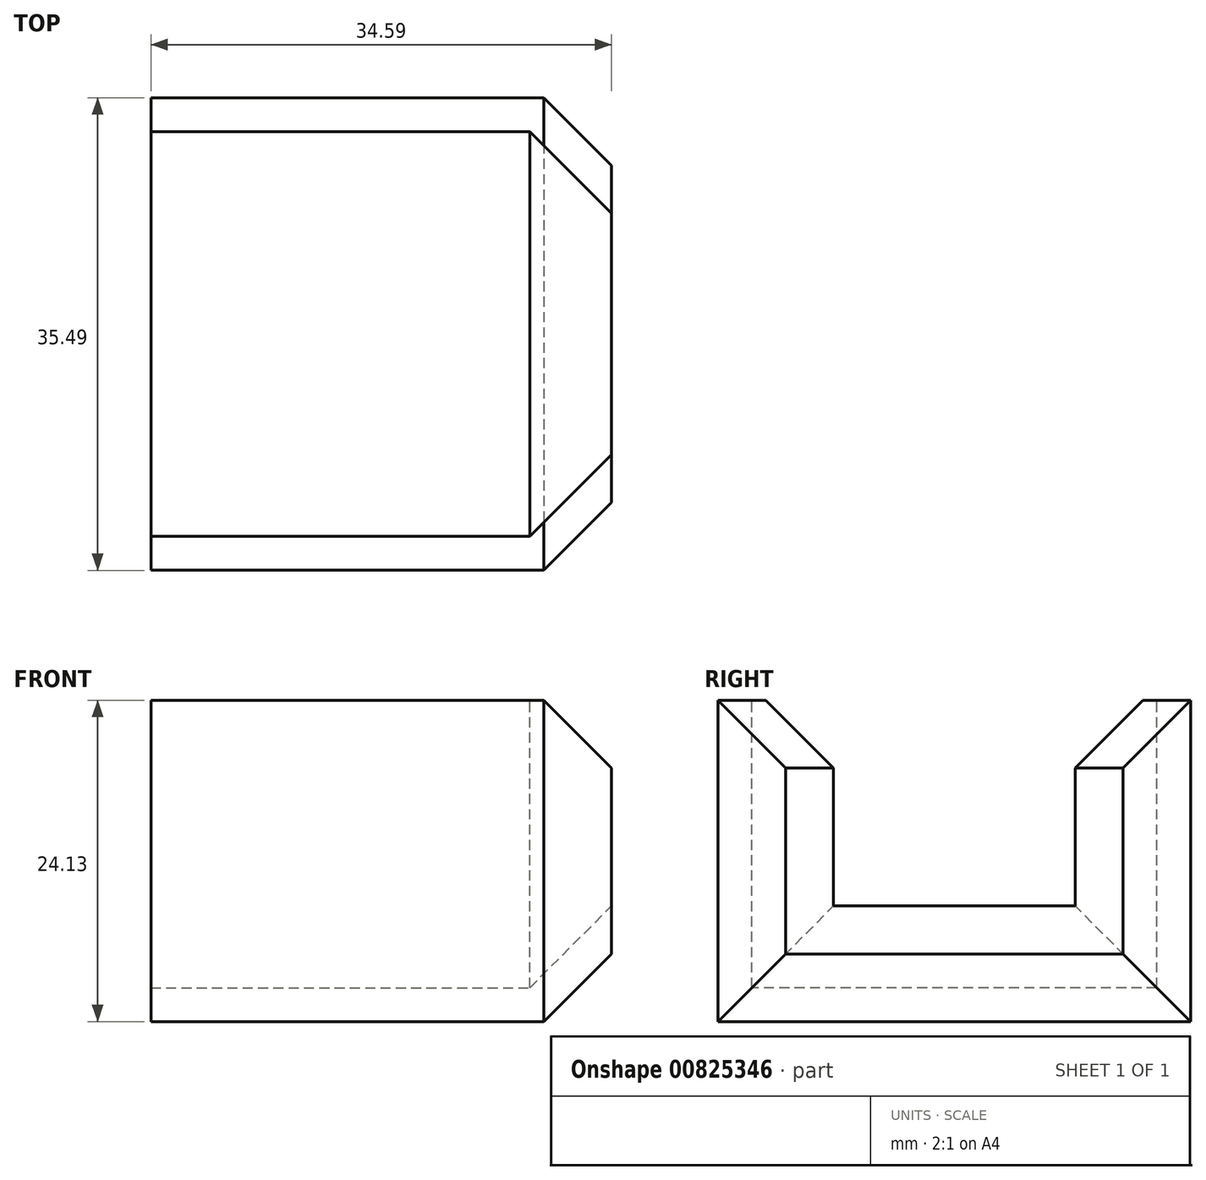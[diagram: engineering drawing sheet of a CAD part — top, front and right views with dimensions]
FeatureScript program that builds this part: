
annotation { "Feature Type Name" : "Feature", "Feature Type Description" : "" }
export const myFeature = defineFeature(function(context is Context, id is Id, definition is map)
    precondition{}
    {
        {
            var Q0;
            Q0=qCreatedBy(makeId("Top.planeOp"),FACE);
            var sketch = newSketch(context, id + "F0", { "sketchPlane" : qUnion([Q0])});
            skLineSegment(sketch, "E0.bottom", {"start": v(-16.4, 28.42) * mm, "end": v(18.2, 28.42) * mm});
            skLineSegment(sketch, "E0.top", {"start": v(-16.4, -7.07) * mm, "end": v(18.2, -7.07) * mm});
            skLineSegment(sketch, "E0.left", {"start": v(-16.4, 28.42) * mm, "end": v(-16.4, -7.07) * mm});
            skLineSegment(sketch, "E0.right", {"start": v(18.2, 28.42) * mm, "end": v(18.2, -7.07) * mm});
            skSolve(sketch);
        }
        {
            var Q0;
            Q0=makeQuery(id+"F0.imprint","IMPRINT",FACE,{"disambiguationData":[TD([[makeQuery(id+"F0.imprint","IMPRINT",EDGE,{"derivedFrom":sQuery(id+"F0.wireOp",EDGE,"E0.bottom")}),-1.0]])]});
            extrude(context, id + "F1", {"entities" : qUnion([Q0]), "oppositeDirection" : true, "depth" : 24.13 * mm, "offsetDistance" : 25.4 * mm});
        }
        {
            var Q0;
            Q0=makeQuery(id+"F1.opExtrude","SWEPT_FACE",FACE,{"disambiguationData":[OSD([sQuery(id+"F0.wireOp",EDGE,"E0.left")])]});
            extrude(context, id + "F2", {"entities" : qUnion([Q0]), "operationType" : NewBodyOperationType.ADD, "oppositeDirection" : true, "depth" : 14.48 * mm, "offsetDistance" : 25.4 * mm});
        }
        {
            var Q0;
            Q0=makeQuery(id+"F1.opExtrude","CAP_EDGE",EDGE,{"disambiguationData":[OSD([sQuery(id+"F0.wireOp",EDGE,"E0.right")])],"isStart":false});
            chamfer(context, id + "F3", {"entities" : qUnion([Q0]), "width" : 5.08 * mm, "tangentPropagation" : true});
        }
        {
            var Q0;
            Q0=makeQuery(id+"F1.opExtrude","CAP_EDGE",EDGE,{"disambiguationData":[OSD([sQuery(id+"F0.wireOp",EDGE,"E0.right")])],"isStart":true});
            chamfer(context, id + "F4", {"entities" : qUnion([Q0]), "width" : 5.08 * mm, "tangentPropagation" : true});
        }
        {
            var Q0;
            Q0=makeQuery(id+"F1.opExtrude","SWEPT_EDGE",EDGE,{"disambiguationData":[OSD([sQuery(id+"F0.wireOp",EDGE,"E0.top"),sQuery(id+"F0.wireOp",EDGE,"E0.right")])]});
            chamfer(context, id + "F5", {"entities" : qUnion([Q0]), "width" : 5.08 * mm, "tangentPropagation" : true});
        }
        {
            var Q0;
            Q0=makeQuery(id+"F1.opExtrude","SWEPT_EDGE",EDGE,{"disambiguationData":[OSD([sQuery(id+"F0.wireOp",EDGE,"E0.bottom"),sQuery(id+"F0.wireOp",EDGE,"E0.right")])]});
            chamfer(context, id + "F6", {"entities" : qUnion([Q0]), "width" : 5.08 * mm, "tangentPropagation" : true});
        }
        {
            var Q0;
            Q0=makeQuery(id+"F4.opChamfer","BLEND_FACE",FACE,{"disambiguationData":[OSD([sQuery(id+"F0.wireOp",EDGE,"E0.right")])]});
            var Q1;
            Q1=makeQuery(id+"F1.opExtrude","CAP_FACE",FACE,{"disambiguationData":[OSD([sQuery(id+"F0.wireOp",EDGE,"E0.bottom"),sQuery(id+"F0.wireOp",EDGE,"E0.top"),sQuery(id+"F0.wireOp",EDGE,"E0.left"),sQuery(id+"F0.wireOp",EDGE,"E0.right")])],"isStart":true});
            var Q2;
            Q2=makeQuery(id+"F1.opExtrude","SWEPT_FACE",FACE,{"disambiguationData":[OSD([sQuery(id+"F0.wireOp",EDGE,"E0.left")])]});
            var Q3;
            Q3=makeQuery(id+"F1.opExtrude","SWEPT_FACE",FACE,{"disambiguationData":[OSD([sQuery(id+"F0.wireOp",EDGE,"E0.right")])]});
            shell(context, id + "F7", {"entities" : qUnion([Q0, Q1, Q2, Q3]), "thickness" : 2.54 * mm});
        }
    });
